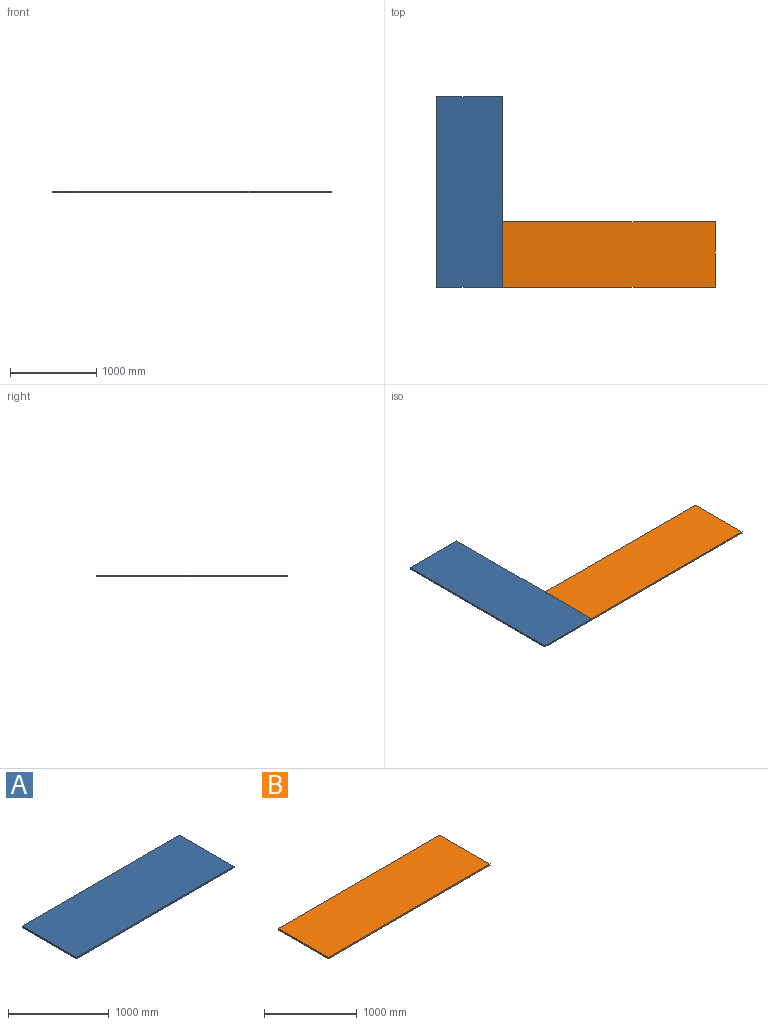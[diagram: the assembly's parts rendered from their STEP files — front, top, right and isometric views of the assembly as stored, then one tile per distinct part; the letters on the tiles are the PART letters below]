
ASSEMBLY  parts=2 mates=3
PART A: 6 faces, bbox 2209.8x762x19.1 mm
  f0: plane 762x19.05mm, normal (-1,0,0), area 14516.1mm2, adj f1,f3,f4,f5
  f1: plane 2209.8x19.05mm, normal (0,-1,0), area 42096.7mm2, adj f0,f2,f4,f5
  f2: plane 762x19.05mm, normal (1,0,0), area 14516.1mm2, adj f1,f3,f4,f5
  f3: plane 2209.8x19.05mm, normal (0,1,0), area 42096.7mm2, adj f0,f2,f4,f5
  f4: plane 2209.8x762mm, normal (0,0,1), area 1683867.6mm2, adj f0,f1,f2,f3
  f5: plane 2209.8x762mm, normal (0,0,-1), area 1683867.6mm2, adj f0,f1,f2,f3
PART B: 6 faces, bbox 2463.8x762x19.1 mm
  f0: plane 762x19.05mm, normal (-1,0,0), area 14516.1mm2, adj f1,f3,f4,f5
  f1: plane 2463.8x19.05mm, normal (0,-1,0), area 46935.4mm2, adj f0,f2,f4,f5
  f2: plane 762x19.05mm, normal (1,0,0), area 14516.1mm2, adj f1,f3,f4,f5
  f3: plane 2463.8x19.05mm, normal (0,1,0), area 46935.4mm2, adj f0,f2,f4,f5
  f4: plane 2463.8x762mm, normal (0,0,1), area 1877415.6mm2, adj f0,f1,f2,f3
  f5: plane 2463.8x762mm, normal (0,0,-1), area 1877415.6mm2, adj f0,f1,f2,f3
PLACE A rot(axis=(0,0,-1),90deg) t=(-485.82,-788.67,-76.31)mm
PLACE B t=(1222.48,-1636,-76.31)mm
MATE planar A.f3 <-> B.f0  axis (1,0,0) through (18.82,-827.36,-66.79)mm
MATE parallel A.f1 <-> B.f0  axis (-1,0,0) through (-743.18,-827.36,-66.79)mm
MATE planar A.f2 <-> B.f1  axis (0,-1,0) through (-362.18,-1932.26,-66.79)mm
